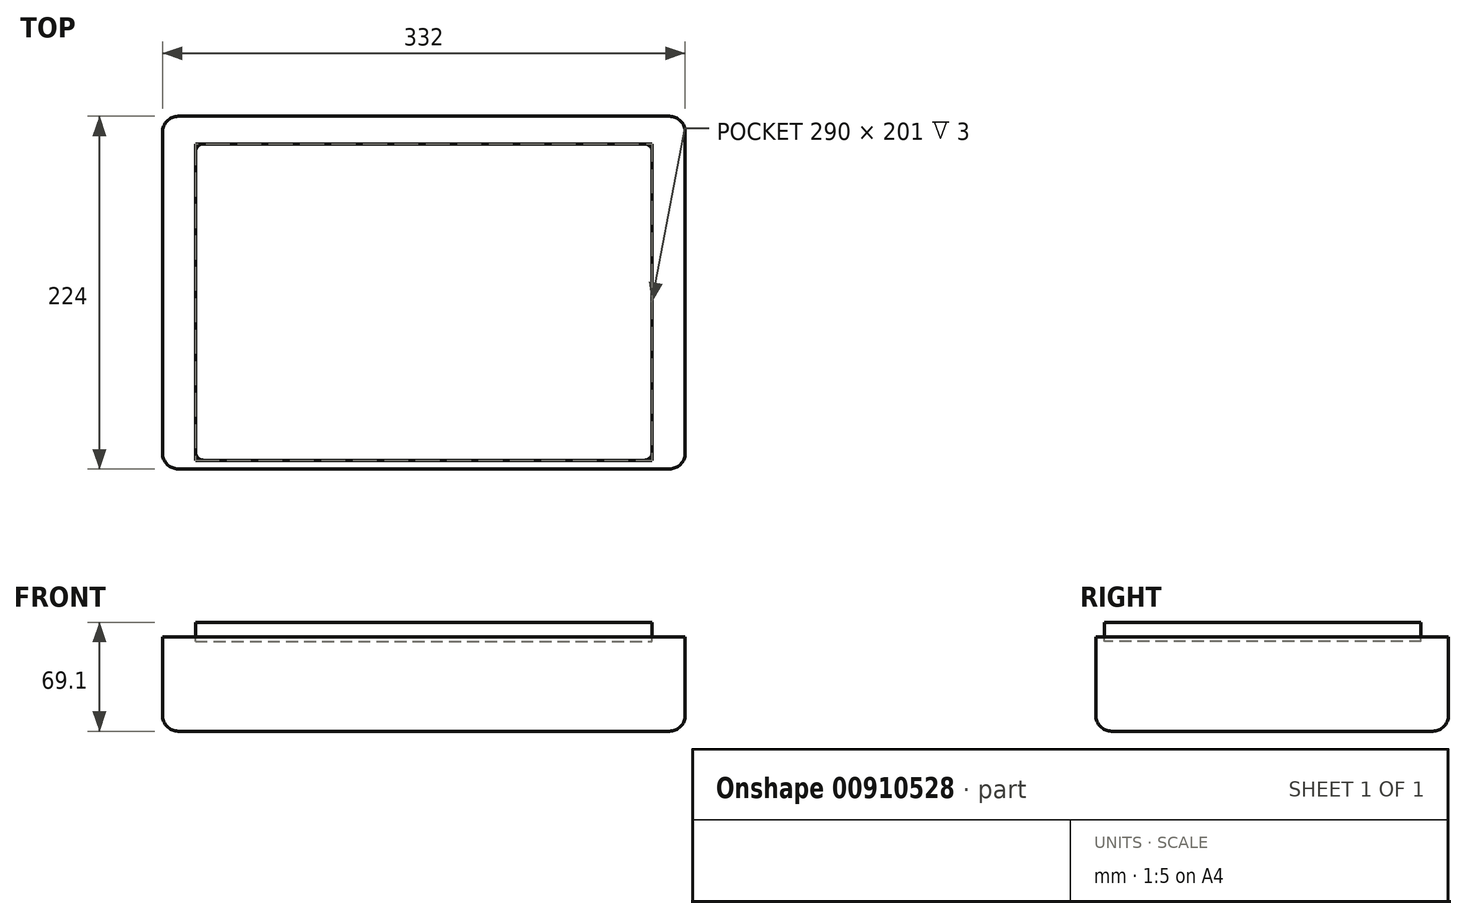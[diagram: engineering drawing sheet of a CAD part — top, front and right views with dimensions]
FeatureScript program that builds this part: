
annotation { "Feature Type Name" : "Feature", "Feature Type Description" : "" }
export const myFeature = defineFeature(function(context is Context, id is Id, definition is map)
    precondition{}
    {
        {
            var Q0;
            Q0=qCreatedBy(makeId("Top.planeOp"),FACE);
            var sketch = newSketch(context, id + "F0", { "sketchPlane" : qUnion([Q0])});
            skLineSegment(sketch, "E0.bottom", {"start": v(-145, 100.5) * mm, "end": v(145, 100.5) * mm});
            skLineSegment(sketch, "E0.top", {"start": v(-145, -100.5) * mm, "end": v(145, -100.5) * mm});
            skLineSegment(sketch, "E0.left", {"start": v(-145, 100.5) * mm, "end": v(-145, -100.5) * mm});
            skLineSegment(sketch, "E0.right", {"start": v(145, 100.5) * mm, "end": v(145, -100.5) * mm});
            skPoint(sketch, "E0.middle", {"position": v(0, 0) * mm});
            skLineSegment(sketch, "E1.bottom", {"start": v(-166, 118) * mm, "end": v(166, 118) * mm});
            skLineSegment(sketch, "E1.top", {"start": v(-166, -106) * mm, "end": v(166, -106) * mm});
            skLineSegment(sketch, "E1.left", {"start": v(-166, 118) * mm, "end": v(-166, -106) * mm});
            skLineSegment(sketch, "E1.right", {"start": v(166, 118) * mm, "end": v(166, -106) * mm});
            skSolve(sketch);
        }
        {
            var Q0;
            Q0=makeQuery(id+"F0.imprint","IMPRINT",FACE,{"disambiguationData":[TD([[makeQuery(id+"F0.imprint","IMPRINT",EDGE,{"derivedFrom":sQuery(id+"F0.wireOp",EDGE,"E0.bottom")}),-1.0]])]});
            var Q1;
            Q1=makeQuery(id+"F0.imprint","IMPRINT",FACE,{"disambiguationData":[TD([[makeQuery(id+"F0.imprint","IMPRINT",EDGE,{"derivedFrom":sQuery(id+"F0.wireOp",EDGE,"E0.bottom")}),1.0]])]});
            extrude(context, id + "F1", {"entities" : qUnion([Q0, Q1]), "oppositeDirection" : true, "depth" : 60 * mm, "offsetDistance" : 25 * mm});
        }
        {
            var Q0;
            Q0=makeQuery(id+"F1.opExtrude","SWEPT_EDGE",EDGE,{"disambiguationData":[OSD([sQuery(id+"F0.wireOp",EDGE,"E1.top"),sQuery(id+"F0.wireOp",EDGE,"E1.right")])]});
            var Q1;
            Q1=makeQuery(id+"F1.opExtrude","SWEPT_EDGE",EDGE,{"disambiguationData":[OSD([sQuery(id+"F0.wireOp",EDGE,"E1.bottom"),sQuery(id+"F0.wireOp",EDGE,"E1.right")])]});
            var Q2;
            Q2=makeQuery(id+"F1.opExtrude","SWEPT_EDGE",EDGE,{"disambiguationData":[OSD([sQuery(id+"F0.wireOp",EDGE,"E1.top"),sQuery(id+"F0.wireOp",EDGE,"E1.left")])]});
            var Q3;
            Q3=makeQuery(id+"F1.opExtrude","CAP_EDGE",EDGE,{"disambiguationData":[OSD([sQuery(id+"F0.wireOp",EDGE,"E1.top")])],"isStart":false});
            var Q4;
            Q4=makeQuery(id+"F1.opExtrude","CAP_EDGE",EDGE,{"disambiguationData":[OSD([sQuery(id+"F0.wireOp",EDGE,"E1.right")])],"isStart":false});
            var Q5;
            Q5=makeQuery(id+"F1.opExtrude","CAP_EDGE",EDGE,{"disambiguationData":[OSD([sQuery(id+"F0.wireOp",EDGE,"E1.left")])],"isStart":false});
            var Q6;
            Q6=makeQuery(id+"F1.opExtrude","CAP_EDGE",EDGE,{"disambiguationData":[OSD([sQuery(id+"F0.wireOp",EDGE,"E1.bottom")])],"isStart":false});
            var Q7;
            Q7=makeQuery(id+"F1.opExtrude","SWEPT_EDGE",EDGE,{"disambiguationData":[OSD([sQuery(id+"F0.wireOp",EDGE,"E1.bottom"),sQuery(id+"F0.wireOp",EDGE,"E1.left")])]});
            fillet(context, id + "F2", {"entities" : qUnion([Q0, Q1, Q2, Q3, Q4, Q5, Q6, Q7]), "radius" : 10 * mm, "tangentPropagation" : true, "allowEdgeOverflow" : false});
        }
        {
            var Q0;
            Q0=makeQuery(id+"F0.imprint","IMPRINT",FACE,{"disambiguationData":[TD([[makeQuery(id+"F0.imprint","IMPRINT",EDGE,{"derivedFrom":sQuery(id+"F0.wireOp",EDGE,"E0.bottom")}),-1.0]])]});
            extrude(context, id + "F3", {"entities" : qUnion([Q0]), "operationType" : NewBodyOperationType.REMOVE, "oppositeDirection" : true, "depth" : 3 * mm, "offsetDistance" : 25 * mm});
        }
        {
            var Q0;
            Q0=makeQuery(id+"F0.imprint","IMPRINT",FACE,{"disambiguationData":[TD([[makeQuery(id+"F0.imprint","IMPRINT",EDGE,{"derivedFrom":sQuery(id+"F0.wireOp",EDGE,"E0.bottom")}),-1.0]])]});
            extrude(context, id + "F4", {"entities" : qUnion([Q0]), "oppositeDirection" : true, "depth" : 2.9 * mm, "offsetDistance" : 25 * mm});
        }
        {
            var Q0;
            Q0=makeQuery(id+"F0.imprint","IMPRINT",FACE,{"disambiguationData":[TD([[makeQuery(id+"F0.imprint","IMPRINT",EDGE,{"derivedFrom":sQuery(id+"F0.wireOp",EDGE,"E0.bottom")}),-1.0]])]});
            extrude(context, id + "F5", {"entities" : qUnion([Q0]), "depth" : 9.1 * mm, "offsetDistance" : 25 * mm});
        }
        {
            var Q0;
            Q0=makeQuery(id+"F5.opExtrude","SWEPT_EDGE",EDGE,{"disambiguationData":[OSD([sQuery(id+"F0.wireOp",EDGE,"E0.top"),sQuery(id+"F0.wireOp",EDGE,"E0.right")])]});
            var Q1;
            Q1=makeQuery(id+"F5.opExtrude","SWEPT_EDGE",EDGE,{"disambiguationData":[OSD([sQuery(id+"F0.wireOp",EDGE,"E0.bottom"),sQuery(id+"F0.wireOp",EDGE,"E0.right")])]});
            var Q2;
            Q2=makeQuery(id+"F5.opExtrude","SWEPT_EDGE",EDGE,{"disambiguationData":[OSD([sQuery(id+"F0.wireOp",EDGE,"E0.top"),sQuery(id+"F0.wireOp",EDGE,"E0.left")])]});
            var Q3;
            Q3=makeQuery(id+"F5.opExtrude","SWEPT_EDGE",EDGE,{"disambiguationData":[OSD([sQuery(id+"F0.wireOp",EDGE,"E0.bottom"),sQuery(id+"F0.wireOp",EDGE,"E0.left")])]});
            fillet(context, id + "F6", {"entities" : qUnion([Q0, Q1, Q2, Q3]), "radius" : 5 * mm, "tangentPropagation" : true, "allowEdgeOverflow" : false});
        }
        {
            var Q0;
            Q0=makeQuery(id+"F1.opExtrude","SWEPT_FACE",FACE,{"disambiguationData":[OSD([sQuery(id+"F0.wireOp",EDGE,"E1.top")])]});
            var sketch = newSketch(context, id + "F7", { "sketchPlane" : qUnion([Q0])});
            skText(sketch, "E2", { "text": "CarryLab", "fontName": "OpenSans-Bold.ttf"});
            const initialGuessF7  = {"E2": [0.1025, -0.0461, 1, 0, 0.00818]};
            skSetInitialGuess(sketch, initialGuessF7);
            skSolve(sketch);
        }
        {
            var Q0;
            Q0 = qSketchRegion(id + "F7", true);
            var Q1;
            Q1 = qConstructionFilter(qBodyType(qCreatedBy(id + "F7" ,EDGE), BodyType.WIRE), ConstructionObject.NO);
            extrude(context, id + "F8", {"entities" : qUnion([Q0]), "bodyType" : ToolBodyType.SURFACE, "surfaceEntities" : qUnion([Q1]), "depth" : 0.1 * mm, "offsetDistance" : 25 * mm});
        }
    });
